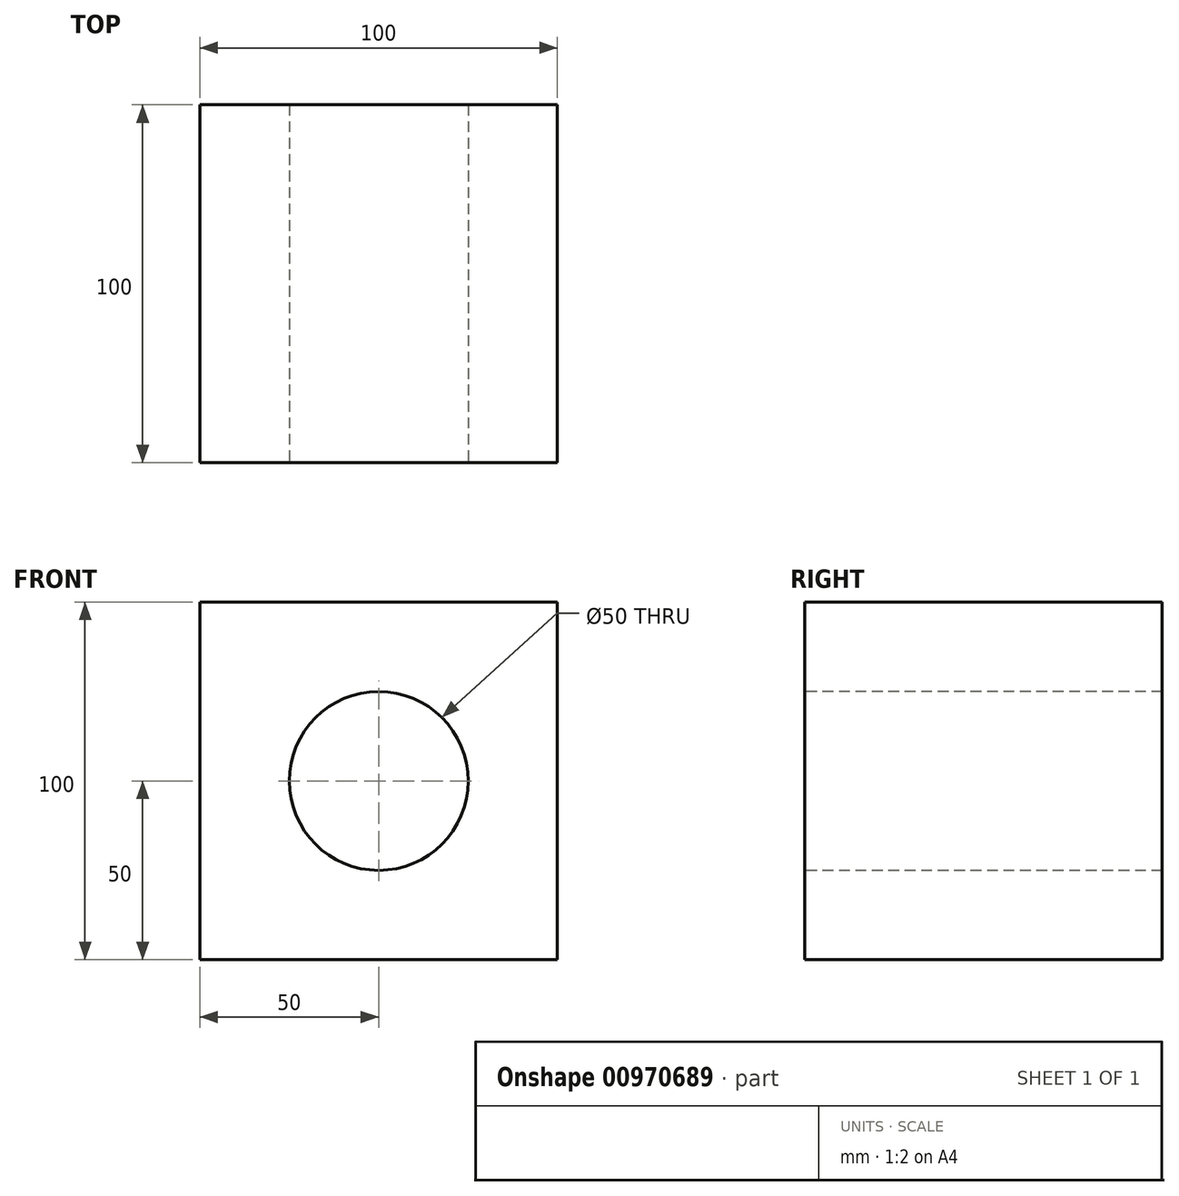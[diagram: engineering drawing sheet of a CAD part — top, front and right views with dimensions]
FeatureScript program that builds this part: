
annotation { "Feature Type Name" : "Feature", "Feature Type Description" : "" }
export const myFeature = defineFeature(function(context is Context, id is Id, definition is map)
    precondition{}
    {
        {
            var Q0;
            Q0=qCreatedBy(makeId("Front.planeOp"),FACE);
            var sketch = newSketch(context, id + "F0", { "sketchPlane" : qUnion([Q0])});
            skLineSegment(sketch, "E0.bottom", {"start": v(50, -50) * mm, "end": v(-50, -50) * mm});
            skLineSegment(sketch, "E0.top", {"start": v(50, 50) * mm, "end": v(-50, 50) * mm});
            skLineSegment(sketch, "E0.left", {"start": v(50, -50) * mm, "end": v(50, 50) * mm});
            skLineSegment(sketch, "E0.right", {"start": v(-50, -50) * mm, "end": v(-50, 50) * mm});
            skPoint(sketch, "E0.middle", {"position": v(0, 0) * mm});
            skSolve(sketch);
        }
        {
            var Q0;
            Q0 = qSketchRegion(id + "F0", true);
            extrude(context, id + "F1", {"entities" : qUnion([Q0]), "endBound" : BoundingType.SYMMETRIC, "depth" : 100 * mm, "offsetDistance" : 25 * mm});
        }
        {
            var Q0;
            Q0=makeQuery(id+"F1.opExtrude","CAP_FACE",FACE,{"disambiguationData":[OSD([sQuery(id+"F0.wireOp",EDGE,"E0.bottom"),sQuery(id+"F0.wireOp",EDGE,"E0.top"),sQuery(id+"F0.wireOp",EDGE,"E0.left"),sQuery(id+"F0.wireOp",EDGE,"E0.right")])],"isStart":false});
            var sketch = newSketch(context, id + "F2", { "sketchPlane" : qUnion([Q0])});
            skCircle(sketch, "E1", {"center": v(0, 0) * mm, "radius": 25 * mm});
            skSolve(sketch);
        }
        {
            var Q0;
            Q0 = qSketchRegion(id + "F2", true);
            extrude(context, id + "F3", {"entities" : qUnion([Q0]), "operationType" : NewBodyOperationType.REMOVE, "endBound" : BoundingType.THROUGH_ALL, "oppositeDirection" : true, "depth" : 25 * mm, "offsetDistance" : 25 * mm});
        }
    });
